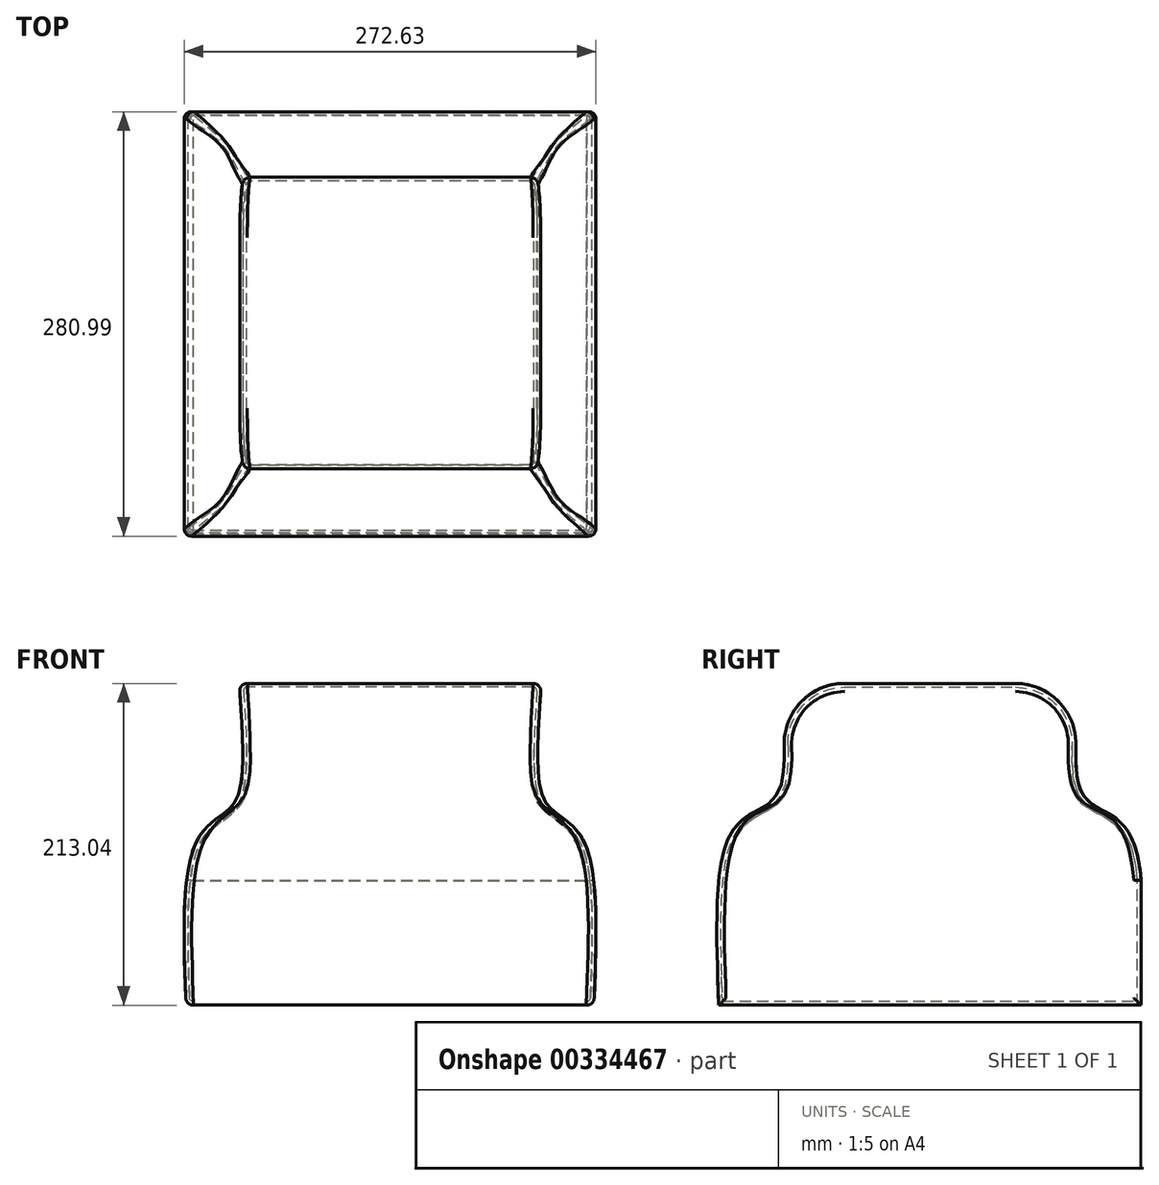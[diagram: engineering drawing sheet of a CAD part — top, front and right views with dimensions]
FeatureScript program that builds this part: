
annotation { "Feature Type Name" : "Feature", "Feature Type Description" : "" }
export const myFeature = defineFeature(function(context is Context, id is Id, definition is map)
    precondition{}
    {
        {
            var Q0;
            Q0=qCreatedBy(makeId("Front.planeOp"),FACE);
            var sketch = newSketch(context, id + "F0", { "sketchPlane" : qUnion([Q0])});
            skFitSpline(sketch, "E0", {"points": [v(35.19, 212.96) * mm, v(35.19, 140.74) * mm, v(25, 126.85) * mm, v(6.48, 107.4) * mm, v(0, 0) * mm], "startDerivative": vector(20.48, -288.84) * mm, "endDerivative": vector(13.55, -353.68) * mm});
            skLineSegment(sketch, "E1", {"start": v(35.19, 212.96) * mm, "end": v(135.19, 212.96) * mm});
            skLineSegment(sketch, "E2", {"start": v(0, 0) * mm, "end": v(135.19, 0) * mm});
            skLineSegment(sketch, "E3.MirrorCS", {"start": v(270, 0) * mm, "end": v(134.81, 0) * mm});
            skFitSpline(sketch, "E4.MirrorCS", {"points": [v(235.19, 212.96) * mm, v(235.19, 140.74) * mm, v(245.37, 126.85) * mm, v(263.89, 107.4) * mm, v(270, 0) * mm], "startDerivative": vector(-20.48, -288.84) * mm, "endDerivative": vector(-13.55, -353.68) * mm});
            skLineSegment(sketch, "E5.MirrorCS", {"start": v(235.19, 212.96) * mm, "end": v(135.19, 212.96) * mm});
            skSolve(sketch);
        }
        {
            var Q0;
            Q0=makeQuery(id+"F0.imprint","IMPRINT",FACE,{"disambiguationData":[TD([[makeQuery(id+"F0.imprint","IMPRINT",EDGE,{"derivedFrom":sQuery(id+"F0.wireOp",EDGE,"E0")}),1.0]])]});
            extrude(context, id + "F1", {"entities" : qUnion([Q0]), "depth" : 300 * mm});
        }
        {
            var Q0;
            Q0=qCreatedBy(makeId("Right.planeOp"),FACE);
            var sketch = newSketch(context, id + "F2", { "sketchPlane" : qUnion([Q0])});
            skLineSegment(sketch, "E6.bottom", {"start": v(0, 0) * mm, "end": v(-300, 0) * mm});
            skLineSegment(sketch, "E6.top", {"start": v(0, 213) * mm, "end": v(-300, 213) * mm});
            skLineSegment(sketch, "E6.left", {"start": v(0, 0) * mm, "end": v(0, 213) * mm});
            skLineSegment(sketch, "E6.right", {"start": v(-300, 0) * mm, "end": v(-300, 213) * mm});
            skSolve(sketch);
        }
        {
            var Q0;
            Q0=qCreatedBy(makeId("Right.planeOp"),FACE);
            var sketch = newSketch(context, id + "F3", { "sketchPlane" : qUnion([Q0])});
            skPoint(sketch, "E7.end.orphan", {"position": v(-139.87, 0) * mm});
            skLineSegment(sketch, "E8", {"start": v(-139.87, 0) * mm, "end": v(-139.87, 213) * mm});
            skPoint(sketch, "E9.0.internal.orphan", {"position": v(-77.4, 211.73) * mm});
            skPoint(sketch, "E9.4.internal.orphan", {"position": v(-42.54, 0) * mm});
            skLineSegment(sketch, "E10", {"start": v(-139.87, 213) * mm, "end": v(-39.87, 213) * mm});
            skSolve(sketch);
        }
        {
            var Q0;
            Q0=makeQuery(id+"F2.imprint","IMPRINT",FACE,{"disambiguationData":[TD([[makeQuery(id+"F2.imprint","IMPRINT",EDGE,{"derivedFrom":sQuery(id+"F2.wireOp",EDGE,"E6.bottom")}),-1.0]])]});
            var sketch = newSketch(context, id + "F4", { "sketchPlane" : qUnion([Q0])});
            skPoint(sketch, "E11.3.internal.orphan", {"position": v(0, 107.67) * mm});
            skFitSpline(sketch, "E12", {"points": [v(-39.87, 213) * mm, v(-39.39, 140.83) * mm, v(-22.8, 127.46) * mm, v(-5.16, 107.67) * mm, v(0, 0) * mm], "startDerivative": vector(-31.92, -302.16) * mm, "endDerivative": vector(-13.04, -358.35) * mm});
            skFitSpline(sketch, "E13.MirrorCS", {"points": [v(-239.87, 213) * mm, v(-240.34, 140.83) * mm, v(-256.92, 127.46) * mm, v(-274.57, 107.67) * mm, v(-279.73, 0) * mm], "startDerivative": vector(31.92, -302.16) * mm, "endDerivative": vector(13.04, -358.35) * mm});
            skSolve(sketch);
        }
        {
            var Q0;
            {var subQ0=sQuery(id+"F4.wireOp",EDGE,"E13.MirrorCS");Q0=makeQuery(id+"F4.imprint","IMPRINT",FACE,{"disambiguationData":[TD([[makeQuery(id+"F4.imprint","IMPRINT",EDGE,{"derivedFrom":subQ0}),-1.0]])]});}
            var Q1;
            {var subQ0=sQuery(id+"F4.wireOp",EDGE,"E12");var subQ1=makeQuery(id+"F2.imprint","IMPRINT",EDGE,{"derivedFrom":sQuery(id+"F2.wireOp",EDGE,"E6.top")});var subQ2=makeQuery(id+"F4.imprint","INTERSECT",VERTEX,{"derivedFrom":[subQ1,subQ0]});Q1=makeQuery(id+"F4.imprint","IMPRINT",FACE,{"disambiguationData":[TD([[makeQuery(id+"F4.imprint","IMPRINT",EDGE,{"disambiguationData":[TD([[subQ2,-1.0]])],"derivedFrom":subQ0}),1.0]])]});}
            extrude(context, id + "F5", {"entities" : qUnion([Q0, Q1]), "operationType" : NewBodyOperationType.REMOVE, "endBound" : BoundingType.SYMMETRIC, "depth" : 700 * mm});
        }
        {
            var Q0;
            Q0=makeQuery(id+"F5.boolean.opBoolean","INTERSECT",EDGE,{"derivedFrom":[makeQuery(id+"F1.opExtrude","SWEPT_FACE",FACE,{"disambiguationData":[OSD([sQuery(id+"F0.wireOp",EDGE,"E1"),sQuery(id+"F0.wireOp",EDGE,"E5.MirrorCS")])]}),makeQuery(id+"F5.opExtrude","SWEPT_FACE",FACE,{"disambiguationData":[OSD([sQuery(id+"F4.wireOp",EDGE,"E12")])]})]});
            var Q1;
            Q1=makeQuery(id+"F5.boolean.opBoolean","INTERSECT",EDGE,{"derivedFrom":[makeQuery(id+"F1.opExtrude","SWEPT_FACE",FACE,{"disambiguationData":[OSD([sQuery(id+"F0.wireOp",EDGE,"E1"),sQuery(id+"F0.wireOp",EDGE,"E5.MirrorCS")])]}),makeQuery(id+"F5.opExtrude","SWEPT_FACE",FACE,{"disambiguationData":[OSD([sQuery(id+"F4.wireOp",EDGE,"E13.MirrorCS")])]})]});
            fillet(context, id + "F6", {"entities" : qUnion([Q0, Q1]), "radius" : 40 * mm, "tangentPropagation" : true, "allowEdgeOverflow" : false});
        }
        {
            var Q0;
            Q0=makeQuery(id+"F1.opExtrude","SWEPT_FACE",FACE,{"disambiguationData":[OSD([sQuery(id+"F0.wireOp",EDGE,"E0")])]});
            var Q1;
            Q1=makeQuery(id+"F1.opExtrude","SWEPT_FACE",FACE,{"disambiguationData":[OSD([sQuery(id+"F0.wireOp",EDGE,"E4.MirrorCS")])]});
            fillet(context, id + "F7", {"entities" : qUnion([Q0, Q1]), "radius" : 5 * mm, "tangentPropagation" : true, "allowEdgeOverflow" : false});
        }
        {
            var Q0;
            Q0=makeQuery(id+"F1.opExtrude","SWEPT_FACE",FACE,{"disambiguationData":[OSD([sQuery(id+"F0.wireOp",EDGE,"E2"),sQuery(id+"F0.wireOp",EDGE,"E3.MirrorCS")])]});
            shell(context, id + "F8", {"entities" : qUnion([Q0]), "thickness" : 2.5 * mm});
        }
    });
